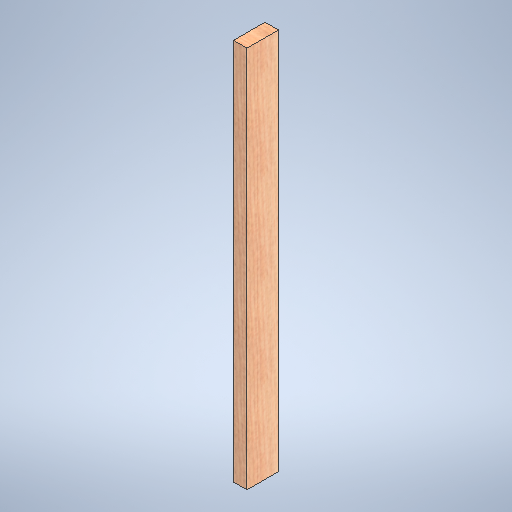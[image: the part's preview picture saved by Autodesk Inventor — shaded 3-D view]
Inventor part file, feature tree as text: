
AUTODESK INVENTOR PART (.ipt)
format: ipt  version: 2025.1 (Build 291241020, 241B)  size: 311,808 bytes
history: native  units: in
note: dims shown in document units (in); Inventor stores cm internally (conversion verified against a paired STEP export)
features: extrude x1, sketch x1
ambient origin geometry x8: Origin, YZ Plane, XZ Plane, XY Plane, X Axis, Y Axis, Z Axis, Center Point
bodies: Solid1 (feature_tree)
feature tree (2):
  extrude  "Extrusion1"  Depth=1.5in
  sketch  "Sketch1"  dims[d0=3.5in d1=1.5in d2=42.5in d3=0.0in]
